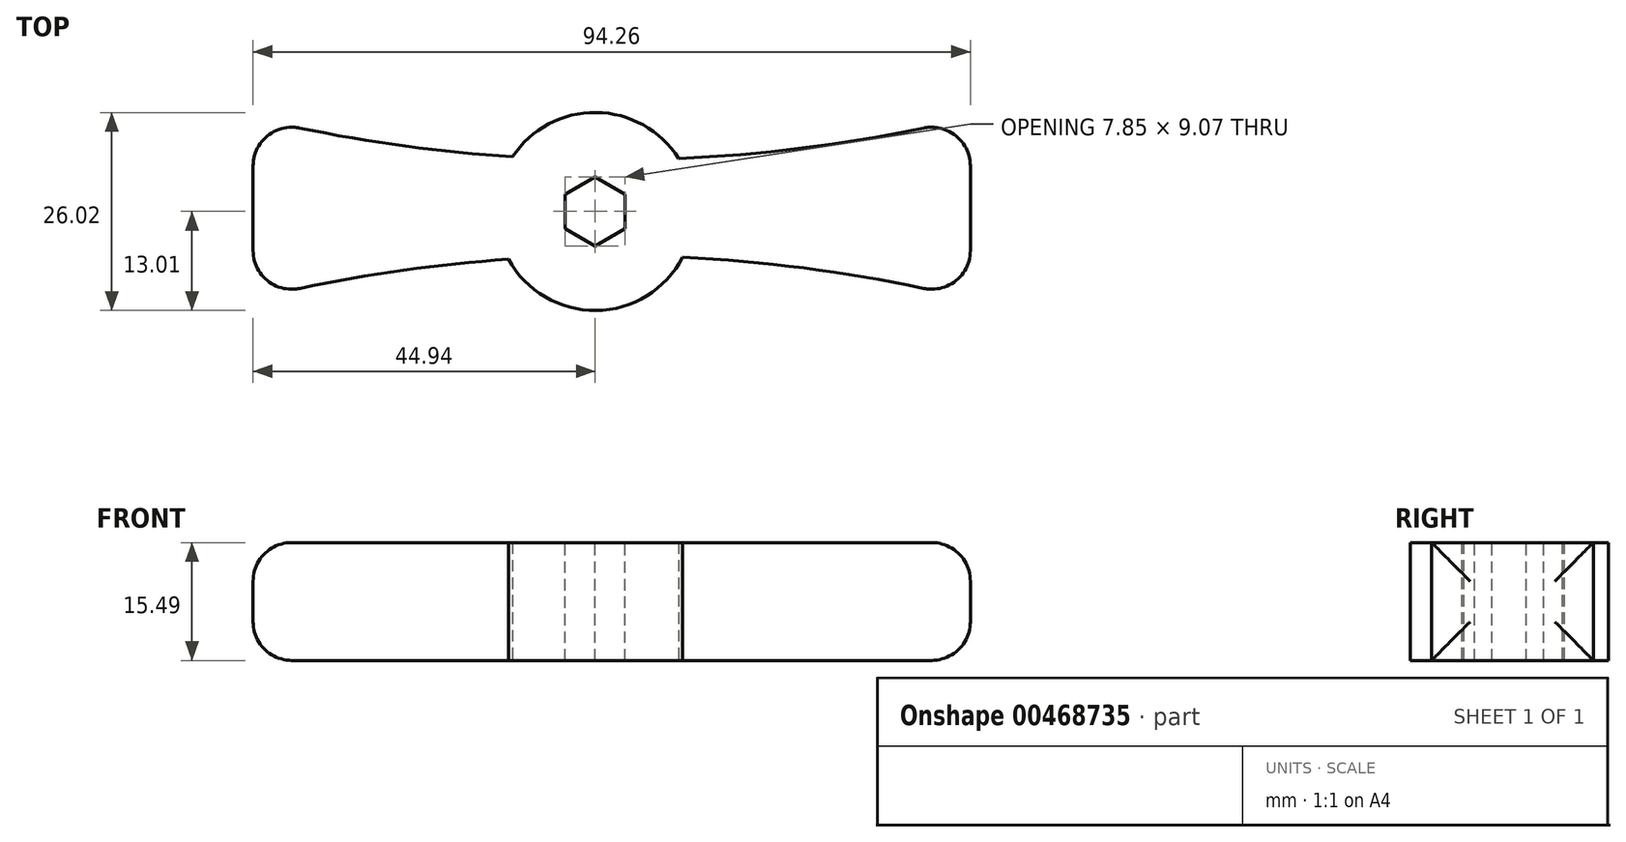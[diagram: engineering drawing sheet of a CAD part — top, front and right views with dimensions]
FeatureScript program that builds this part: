
annotation { "Feature Type Name" : "Feature", "Feature Type Description" : "" }
export const myFeature = defineFeature(function(context is Context, id is Id, definition is map)
    precondition{}
    {
        {
            var Q0;
            Q0=qCreatedBy(makeId("Top.planeOp"),FACE);
            var sketch = newSketch(context, id + "F0", { "sketchPlane" : qUnion([Q0])});
            skLineSegment(sketch, "E0.left", {"start": v(-44.94, 12.33) * mm, "end": v(-44.94, -11.5) * mm});
            skLineSegment(sketch, "E0.right", {"start": v(49.32, 12.33) * mm, "end": v(49.32, -11.5) * mm});
            skArc(sketch, "E1", {"start": v(49.32, -11.5) * mm, "mid": v(2.2, -5.82) * mm, "end": v(-44.94, -11.5) * mm});
            skArc(sketch, "E2", {"start": v(-44.94, 12.33) * mm, "mid": v(2.2, 6.76) * mm, "end": v(49.32, 12.33) * mm});
            skCircle(sketch, "E3", {"center": v(0, 0) * mm, "radius": 13 * mm});
            skSolve(sketch);
        }
        {
            var Q0;
            Q0 = qSketchRegion(id + "F0", true);
            extrude(context, id + "F1", {"entities" : qUnion([Q0]), "depth" : 15.5 * mm});
        }
        {
            var Q0;
            Q0=makeQuery(id+"F1.opExtrude","CAP_EDGE",EDGE,{"disambiguationData":[OSD([sQuery(id+"F0.wireOp",EDGE,"E0.top")])],"isStart":false});
            var Q1;
            Q1=makeQuery(id+"F1.opExtrude","CAP_EDGE",EDGE,{"disambiguationData":[OSD([sQuery(id+"F0.wireOp",EDGE,"E0.bottom")])],"isStart":false});
            var Q2;
            Q2=makeQuery(id+"F1.opExtrude","CAP_EDGE",EDGE,{"disambiguationData":[OSD([sQuery(id+"F0.wireOp",EDGE,"E0.left")])],"isStart":false});
            var Q3;
            Q3=makeQuery(id+"F1.opExtrude","CAP_EDGE",EDGE,{"disambiguationData":[OSD([sQuery(id+"F0.wireOp",EDGE,"E0.right")])],"isStart":false});
            var Q4;
            Q4=makeQuery(id+"F1.opExtrude","CAP_EDGE",EDGE,{"disambiguationData":[OSD([sQuery(id+"F0.wireOp",EDGE,"E0.left")])],"isStart":true});
            var Q5;
            Q5=makeQuery(id+"F1.opExtrude","CAP_EDGE",EDGE,{"disambiguationData":[OSD([sQuery(id+"F0.wireOp",EDGE,"E0.right")])],"isStart":true});
            var Q6;
            Q6=makeQuery(id+"F1.opExtrude","SWEPT_EDGE",EDGE,{"disambiguationData":[OSD([sQuery(id+"F0.wireOp",EDGE,"E0.top"),sQuery(id+"F0.wireOp",EDGE,"E0.left")])]});
            var Q7;
            Q7=makeQuery(id+"F1.opExtrude","SWEPT_EDGE",EDGE,{"disambiguationData":[OSD([sQuery(id+"F0.wireOp",EDGE,"E0.top"),sQuery(id+"F0.wireOp",EDGE,"E0.right")])]});
            var Q8;
            Q8=makeQuery(id+"F1.opExtrude","SWEPT_EDGE",EDGE,{"disambiguationData":[OSD([sQuery(id+"F0.wireOp",EDGE,"E0.bottom"),sQuery(id+"F0.wireOp",EDGE,"E0.left")])]});
            var Q9;
            Q9=makeQuery(id+"F1.opExtrude","SWEPT_EDGE",EDGE,{"disambiguationData":[OSD([sQuery(id+"F0.wireOp",EDGE,"E0.bottom"),sQuery(id+"F0.wireOp",EDGE,"E0.right")])]});
            var Q10;
            Q10=makeQuery(id+"F1.opExtrude","CAP_EDGE",EDGE,{"disambiguationData":[OSD([sQuery(id+"F0.wireOp",EDGE,"E0.bottom")])],"isStart":true});
            var Q11;
            Q11=makeQuery(id+"F1.opExtrude","CAP_EDGE",EDGE,{"disambiguationData":[OSD([sQuery(id+"F0.wireOp",EDGE,"E0.top")])],"isStart":true});
            fillet(context, id + "F2", {"entities" : qUnion([Q0, Q1, Q2, Q3, Q4, Q5, Q6, Q7, Q8, Q9, Q10, Q11]), "radius" : 5.08 * mm, "tangentPropagation" : true, "allowEdgeOverflow" : false});
        }
        {
            var Q0;
            Q0=makeQuery(id+"F1.opExtrude","CAP_FACE",FACE,{"disambiguationData":[OSD([sQuery(id+"F0.wireOp",EDGE,"E0.bottom"),sQuery(id+"F0.wireOp",EDGE,"E0.top"),sQuery(id+"F0.wireOp",EDGE,"E0.left"),sQuery(id+"F0.wireOp",EDGE,"E0.right")])],"isStart":false});
            var sketch = newSketch(context, id + "F3", { "sketchPlane" : qUnion([Q0])});
            skCircle(sketch, "E4.cCircle", {"center": v(0, 0) * mm, "radius": 3.93 * mm, "construction": true});
            skLineSegment(sketch, "E4.0", {"start": v(3.93, 2.27) * mm, "end": v(3.93, -2.27) * mm});
            skLineSegment(sketch, "E4.1", {"start": v(3.93, -2.27) * mm, "end": v(0, -4.53) * mm});
            skLineSegment(sketch, "E4.2", {"start": v(0, -4.53) * mm, "end": v(-3.93, -2.27) * mm});
            skLineSegment(sketch, "E4.3", {"start": v(-3.93, -2.27) * mm, "end": v(-3.93, 2.27) * mm});
            skLineSegment(sketch, "E4.4", {"start": v(-3.93, 2.27) * mm, "end": v(0, 4.53) * mm});
            skLineSegment(sketch, "E4.5", {"start": v(0, 4.53) * mm, "end": v(3.93, 2.27) * mm});
            skPoint(sketch, "E4.0.midPoint", {"position": v(3.93, 0) * mm});
            skSolve(sketch);
        }
        {
            var Q0;
            Q0 = qSketchRegion(id + "F3", true);
            extrude(context, id + "F4", {"entities" : qUnion([Q0]), "operationType" : NewBodyOperationType.REMOVE, "endBound" : BoundingType.THROUGH_ALL, "oppositeDirection" : true, "depth" : 32.6 * mm});
        }
    });
